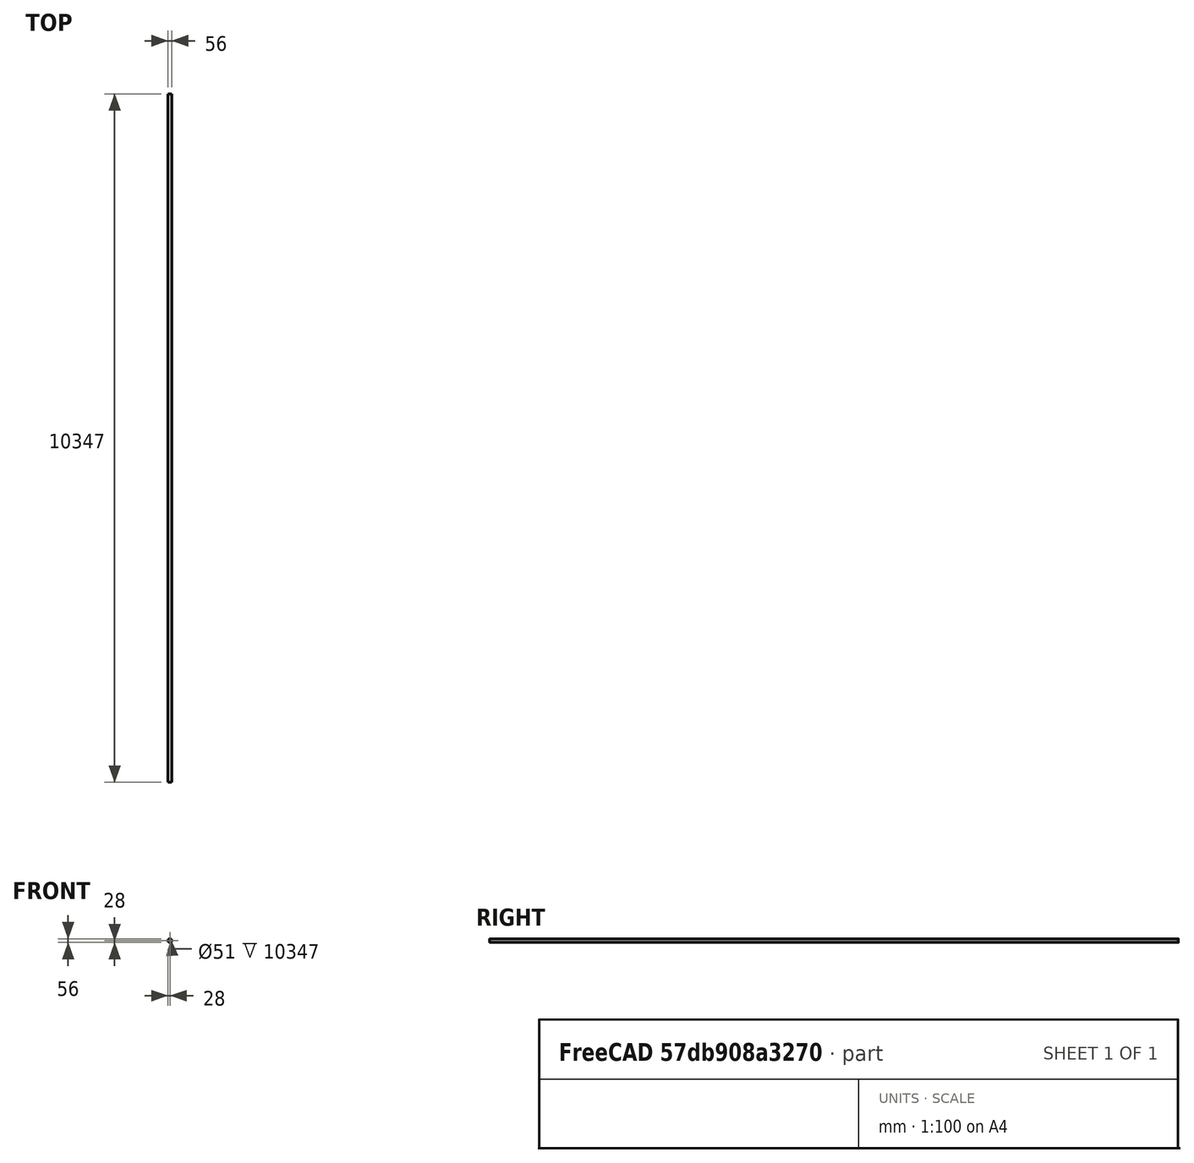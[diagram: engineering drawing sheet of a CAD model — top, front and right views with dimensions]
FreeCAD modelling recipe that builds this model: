
FCSTD DOCUMENT  (FreeCAD 0.18R16131 (Git))
Label: CPC_Fig_3
License: All rights reserved
LicenseURL: http://en.wikipedia.org/wiki/All_rights_reserved
objects: Part::Feature×2, Part::Extrusion×2, Part::Cylinder×2, Part::Cut×1
note: 7 computed .brp shape members not serialized (recipe doc carries the construction recipe); baked Part::Feature solids carry a one-line shape summary decoded from their .brp

FEATURE [Part::Feature] Parabola
  Placement = pos=(0,0,0) rot=(0.57735,-0.57735,0.57735;2.0944rad)
  shape: bbox 1845 x 2e-07 x 328.8 mm, 0 faces, 0 solids (baked)
FEATURE [Part::Extrusion] Extruded_parabola  label="Parabolic_reflector(Mir1)"
  Base = -> Parabola
  Dir = (0,10347,0)
  DirMode = 0
  FaceMakerClass = Part::FaceMakerExtrusion
  LengthFwd = 0
  LengthRev = 0
  Solid = false
  Symmetric = false
FEATURE [Part::Feature] circle_abs_Part
  shape: bbox 34 x 2e-07 x 34 mm, 0 faces, 0 solids (baked)
FEATURE [Part::Extrusion] Abs_circle_abs_Extrude  label="Cylindrical_absorber(Abs1)"
  Base = -> circle_abs_Part
  Dir = (0,10347,0)
  DirMode = 0
  FaceMakerClass = Part::FaceMakerExtrusion
  LengthFwd = 0
  LengthRev = 0
  Solid = false
  Symmetric = false
FEATURE [Part::Cylinder] cylinder_out
  Angle = 360
  AttacherType = Attacher::AttachEngine3D
  Height = 10347
  Placement = pos=(0,0,647) rot=(-1,0,0;1.5708rad)
  Radius = 28
FEATURE [Part::Cylinder] cylinder_in
  Angle = 360
  AttacherType = Attacher::AttachEngine3D
  Height = 10349
  Placement = pos=(0,-1,647) rot=(-1,0,0;1.5708rad)
  Radius = 25.5
FEATURE [Part::Cut] tube_glass  label="Tube_glass(Glass1)"
  Base = -> cylinder_out
  Tool = -> cylinder_in
